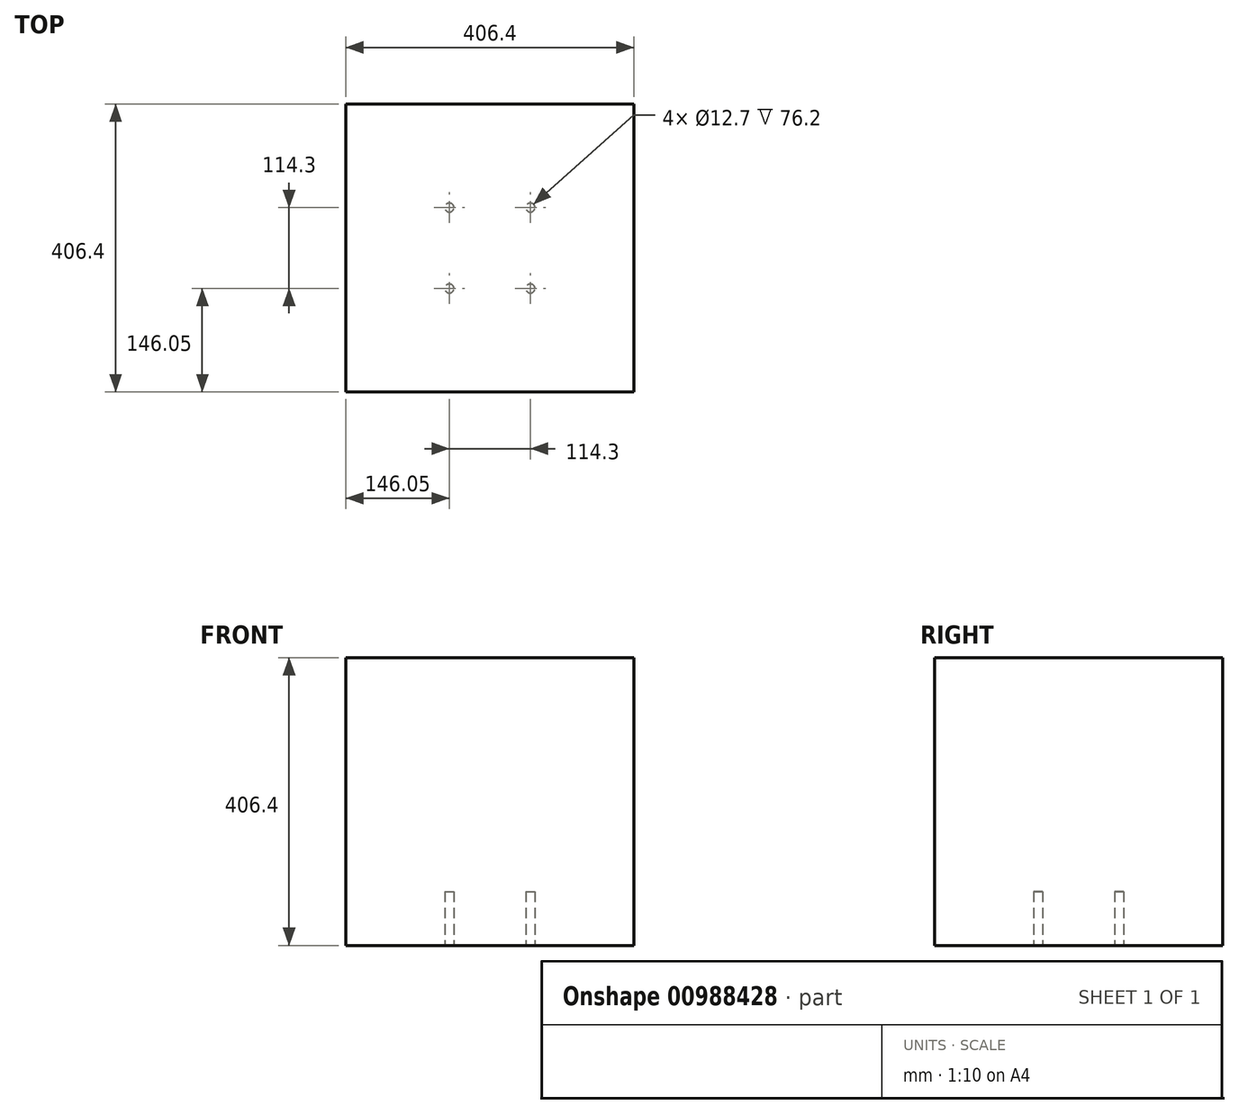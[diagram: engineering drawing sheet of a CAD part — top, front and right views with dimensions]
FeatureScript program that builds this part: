
annotation { "Feature Type Name" : "Feature", "Feature Type Description" : "" }
export const myFeature = defineFeature(function(context is Context, id is Id, definition is map)
    precondition{}
    {
        {
            assignVariable(context, id + "F0", {"name" : "WeightDepth", "anyValue" : 406.4 * mm});
        }
        {
            var Q0;
            Q0=qCreatedBy(makeId("Top.planeOp"),FACE);
            var sketch = newSketch(context, id + "F1", { "sketchPlane" : qUnion([Q0])});
            skLineSegment(sketch, "E0.bottom", {"start": v(203.2, -203.2) * mm, "end": v(-203.2, -203.2) * mm});
            skLineSegment(sketch, "E0.top", {"start": v(203.2, 203.2) * mm, "end": v(-203.2, 203.2) * mm});
            skLineSegment(sketch, "E0.left", {"start": v(203.2, -203.2) * mm, "end": v(203.2, 203.2) * mm});
            skLineSegment(sketch, "E0.right", {"start": v(-203.2, -203.2) * mm, "end": v(-203.2, 203.2) * mm});
            skPoint(sketch, "E0.middle", {"position": v(0, 0) * mm});
            skSolve(sketch);
        }
        {
            var Q0;
            Q0 = qSketchRegion(id + "F1", true);
            extrude(context, id + "F2", {"entities" : qUnion([Q0]), "depth" : getVariable(context, 'WeightDepth'), "offsetDistance" : 25.4 * mm});
        }
        {
            var Q0;
            Q0=makeQuery(id+"F2.opExtrude","CAP_FACE",FACE,{"disambiguationData":[OSD([sQuery(id+"F1.wireOp",EDGE,"E0.bottom"),sQuery(id+"F1.wireOp",EDGE,"E0.top"),sQuery(id+"F1.wireOp",EDGE,"E0.left"),sQuery(id+"F1.wireOp",EDGE,"E0.right")])],"isStart":true});
            var sketch = newSketch(context, id + "F3", { "sketchPlane" : qUnion([Q0])});
            skCircle(sketch, "E1", {"center": v(57.15, 57.15) * mm, "radius": 6.35 * mm});
            skCircle(sketch, "E2", {"center": v(57.15, -57.15) * mm, "radius": 6.35 * mm});
            skCircle(sketch, "E3", {"center": v(-57.15, -57.15) * mm, "radius": 6.35 * mm});
            skCircle(sketch, "E4", {"center": v(-57.15, 57.15) * mm, "radius": 6.35 * mm});
            skSolve(sketch);
        }
        {
            var Q0;
            Q0 = qSketchRegion(id + "F3", true);
            extrude(context, id + "F4", {"entities" : qUnion([Q0]), "operationType" : NewBodyOperationType.REMOVE, "oppositeDirection" : true, "depth" : 76.2 * mm, "offsetDistance" : 25.4 * mm});
        }
    });
